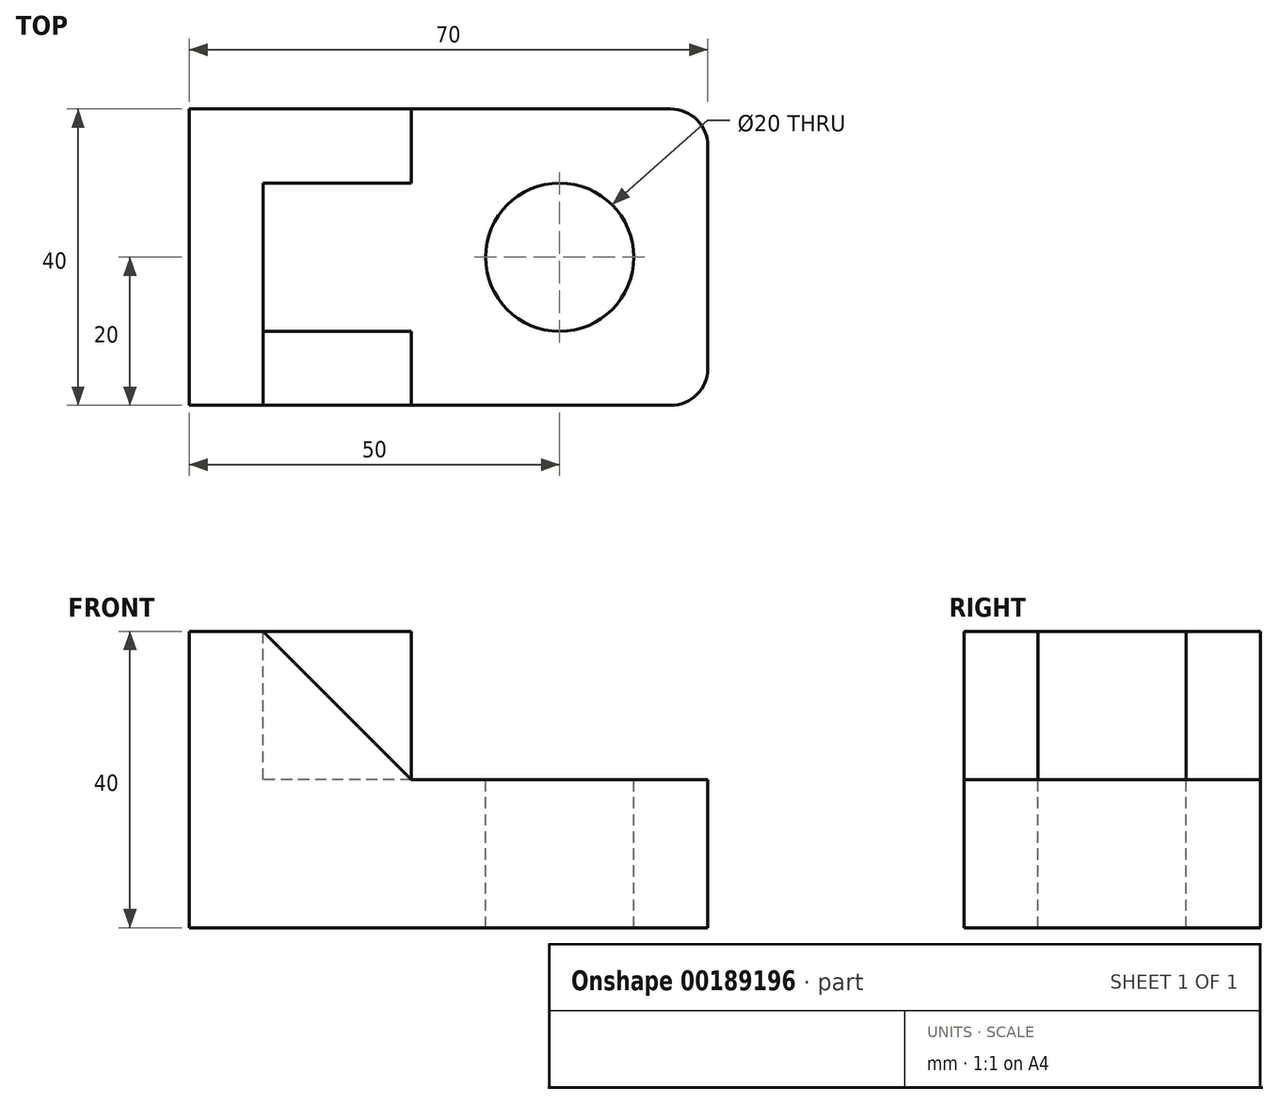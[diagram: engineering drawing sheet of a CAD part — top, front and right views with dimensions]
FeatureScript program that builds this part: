
annotation { "Feature Type Name" : "Feature", "Feature Type Description" : "" }
export const myFeature = defineFeature(function(context is Context, id is Id, definition is map)
    precondition{}
    {
        {
            var Q0;
            Q0=qCreatedBy(makeId("Front.planeOp"),FACE);
            var sketch = newSketch(context, id + "F0", { "sketchPlane" : qUnion([Q0])});
            skLineSegment(sketch, "E0", {"start": v(0, 0) * mm, "end": v(70, 0) * mm});
            skLineSegment(sketch, "E1", {"start": v(70, 0) * mm, "end": v(70, 20) * mm});
            skLineSegment(sketch, "E2", {"start": v(70, 20) * mm, "end": v(30, 20) * mm});
            skLineSegment(sketch, "E3", {"start": v(30, 20) * mm, "end": v(30, 40) * mm});
            skLineSegment(sketch, "E4", {"start": v(30, 40) * mm, "end": v(0, 40) * mm});
            skLineSegment(sketch, "E5", {"start": v(0, 40) * mm, "end": v(0, 0) * mm});
            skSolve(sketch);
        }
        {
            var Q0;
            Q0=makeQuery(id+"F0.imprint","IMPRINT",FACE,{"disambiguationData":[TD([[makeQuery(id+"F0.imprint","IMPRINT",EDGE,{"derivedFrom":sQuery(id+"F0.wireOp",EDGE,"E0")}),1.0]])]});
            extrude(context, id + "F1", {"entities" : qUnion([Q0]), "depth" : 40 * mm});
        }
        {
            var Q0;
            Q0=makeQuery(id+"F1.opExtrude","SWEPT_FACE",FACE,{"disambiguationData":[OSD([sQuery(id+"F0.wireOp",EDGE,"E4")])]});
            var sketch = newSketch(context, id + "F2", { "sketchPlane" : qUnion([Q0])});
            skLineSegment(sketch, "E6", {"start": v(30, -10) * mm, "end": v(10, -10) * mm});
            skLineSegment(sketch, "E7", {"start": v(10, -10) * mm, "end": v(10, -30) * mm});
            skLineSegment(sketch, "E8", {"start": v(10, -30) * mm, "end": v(30, -30) * mm});
            skSolve(sketch);
        }
        {
            var Q0;
            {var subQ0=sQuery(id+"F2.wireOp",EDGE,"E6");Q0=makeQuery(id+"F2.imprint","IMPRINT",FACE,{"disambiguationData":[TD([[makeQuery(id+"F2.imprint","IMPRINT",EDGE,{"derivedFrom":subQ0}),1.0]])]});}
            var Q1;
            Q1=makeQuery(id+"F1.opExtrude","SWEPT_FACE",FACE,{"disambiguationData":[OSD([sQuery(id+"F0.wireOp",EDGE,"E2")])]});
            extrude(context, id + "F3", {"entities" : qUnion([Q0]), "operationType" : NewBodyOperationType.REMOVE, "endBound" : BoundingType.UP_TO_SURFACE, "oppositeDirection" : true, "endBoundEntityFace" : qUnion([Q1]), "depth" : 25 * mm});
        }
        {
            var Q0;
            Q0=makeQuery(id+"F1.opExtrude","CAP_FACE",FACE,{"disambiguationData":[OSD([sQuery(id+"F0.wireOp",EDGE,"E0"),sQuery(id+"F0.wireOp",EDGE,"E1"),sQuery(id+"F0.wireOp",EDGE,"E2"),sQuery(id+"F0.wireOp",EDGE,"E3"),sQuery(id+"F0.wireOp",EDGE,"E4"),sQuery(id+"F0.wireOp",EDGE,"E5")])],"isStart":false});
            var sketch = newSketch(context, id + "F4", { "sketchPlane" : qUnion([Q0])});
            skLineSegment(sketch, "E9", {"start": v(30, 20) * mm, "end": v(10, 40) * mm});
            skSolve(sketch);
        }
        {
            var Q0;
            {var subQ0=sQuery(id+"F4.wireOp",EDGE,"E9");Q0=makeQuery(id+"F4.imprint","IMPRINT",FACE,{"disambiguationData":[TD([[makeQuery(id+"F4.imprint","IMPRINT",EDGE,{"derivedFrom":subQ0}),-1.0]])]});}
            extrude(context, id + "F5", {"entities" : qUnion([Q0]), "operationType" : NewBodyOperationType.REMOVE, "endBound" : BoundingType.UP_TO_NEXT, "oppositeDirection" : true, "depth" : 25 * mm});
        }
        {
            var Q0;
            {var subQ0=sQuery(id+"F0.wireOp",EDGE,"E2");Q0=makeQuery(id+"F3.boolean.opBoolean","MERGE",FACE,{"derivedFrom":[makeQuery(id+"F1.opExtrude","SWEPT_FACE",FACE,{"disambiguationData":[OSD([subQ0])]}),makeQuery(id+"F3.opExtrude","CAP_FACE",FACE,{"disambiguationData":[OSD([subQ0])],"isStart":false})]});}
            var sketch = newSketch(context, id + "F6", { "sketchPlane" : qUnion([Q0])});
            skPoint(sketch, "E10", {"position": v(50, -20) * mm});
            skSolve(sketch);
        }
        {
            var Q0;
            Q0=sQuery(id+"F6.wireOp",VERTEX,"E10");
            var Q1;
            Q1=makeQuery(id+"F1.opExtrude","SWEPT_BODY",BODY,{"disambiguationData":[OSD([sQuery(id+"F0.wireOp",EDGE,"E0"),sQuery(id+"F0.wireOp",EDGE,"E1"),sQuery(id+"F0.wireOp",EDGE,"E2"),sQuery(id+"F0.wireOp",EDGE,"E3"),sQuery(id+"F0.wireOp",EDGE,"E4"),sQuery(id+"F0.wireOp",EDGE,"E5")])]});
            hole(context, id + "F7", {"style" : HoleStyle.SIMPLE, "endStyle" : HoleEndStyle.THROUGH, "holeDiameter" : 20 * mm, "locations" : qUnion([Q0]), "scope" : qUnion([Q1]), "isTappedThrough" : true});
        }
        {
            var Q0;
            Q0=makeQuery(id+"F1.opExtrude","CAP_EDGE",EDGE,{"disambiguationData":[OSD([sQuery(id+"F0.wireOp",EDGE,"E1")])],"isStart":false});
            var Q1;
            Q1=makeQuery(id+"F1.opExtrude","CAP_EDGE",EDGE,{"disambiguationData":[OSD([sQuery(id+"F0.wireOp",EDGE,"E1")])],"isStart":true});
            fillet(context, id + "F8", {"entities" : qUnion([Q0, Q1]), "radius" : 5 * mm, "tangentPropagation" : true, "allowEdgeOverflow" : false});
        }
    });
